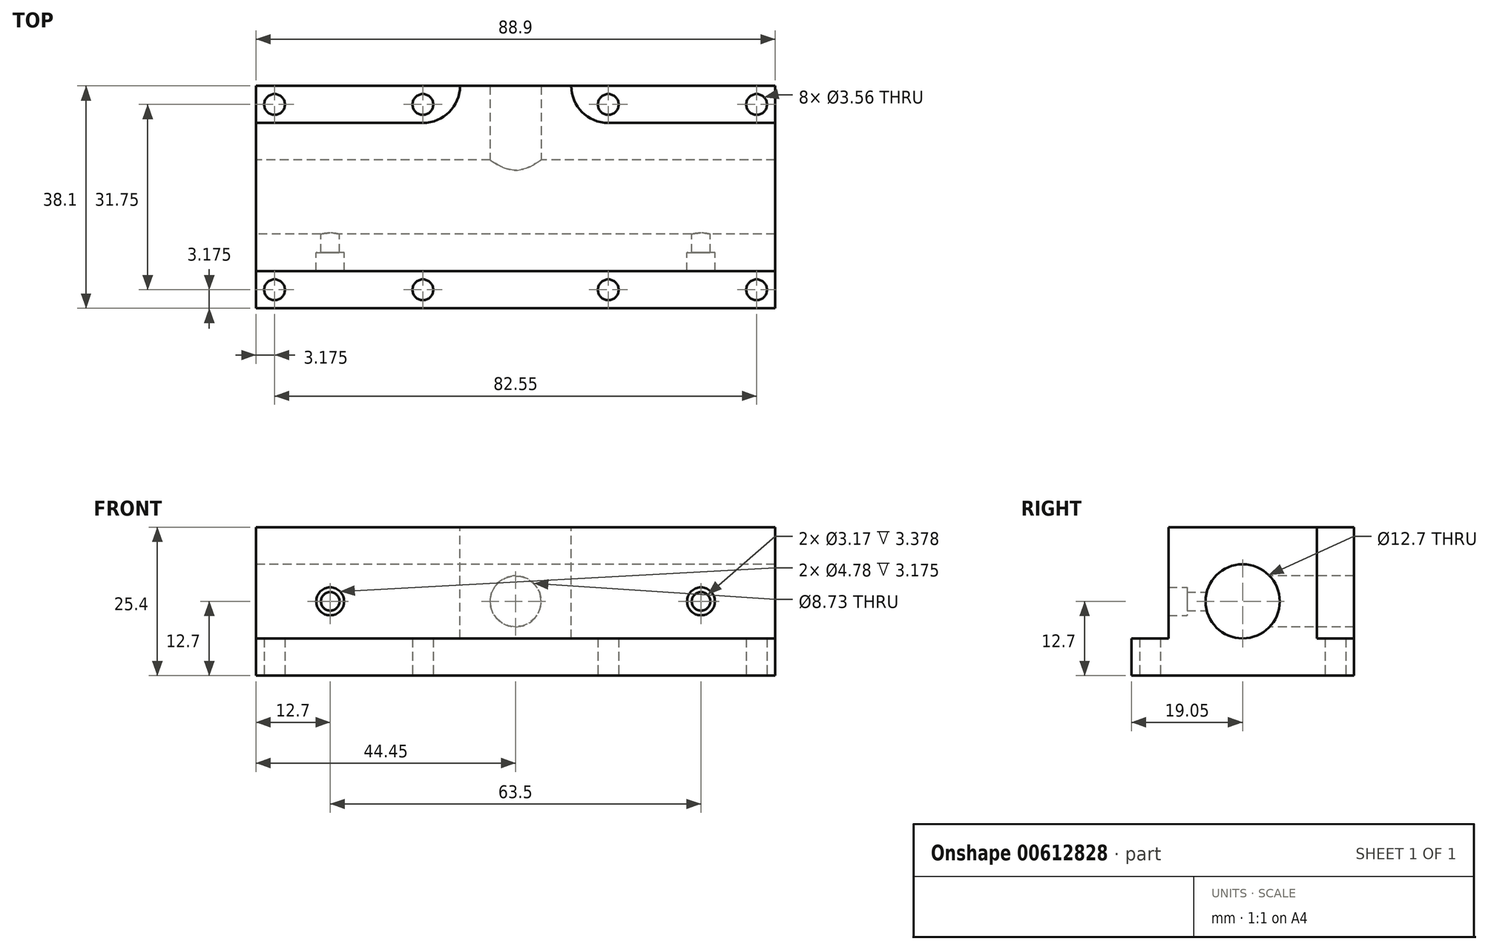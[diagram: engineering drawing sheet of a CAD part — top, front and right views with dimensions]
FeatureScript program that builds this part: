
annotation { "Feature Type Name" : "Feature", "Feature Type Description" : "" }
export const myFeature = defineFeature(function(context is Context, id is Id, definition is map)
    precondition{}
    {
        {
            var Q0;
            Q0=qCreatedBy(makeId("Right.planeOp"),FACE);
            var sketch = newSketch(context, id + "F0", { "sketchPlane" : qUnion([Q0])});
            skLineSegment(sketch, "E0.bottom", {"start": v(-19.05, -12.7) * mm, "end": v(19.05, -12.7) * mm});
            skLineSegment(sketch, "E0.top", {"start": v(-19.05, 12.7) * mm, "end": v(19.05, 12.7) * mm});
            skLineSegment(sketch, "E0.left", {"start": v(-19.05, -12.7) * mm, "end": v(-19.05, 12.7) * mm});
            skLineSegment(sketch, "E0.right", {"start": v(19.05, -12.7) * mm, "end": v(19.05, 12.7) * mm});
            skPoint(sketch, "E1", {"position": v(0, 12.7) * mm});
            skPoint(sketch, "E2", {"position": v(19.05, 0) * mm});
            skCircle(sketch, "E3", {"center": v(0, 0) * mm, "radius": 6.35 * mm});
            skSolve(sketch);
        }
        {
            var Q0;
            Q0=qSketchRegion(id+"F0",true);
            extrude(context, id + "F1", {"entities" : qUnion([Q0]), "depth" : 88.9 * mm, "symmetric" : true});
        }
        {
            var Q0;
            Q0=makeQuery(id+"F1.opExtrude","SWEPT_FACE",FACE,{"disambiguationData":[OSD([sQuery(id+"F0.wireOp",EDGE,"E0.top")])]});
            var sketch = newSketch(context, id + "F2", { "sketchPlane" : qUnion([Q0])});
            skLineSegment(sketch, "E4.bottom", {"start": v(-44.45, 19.05) * mm, "end": v(-9.53, 19.05) * mm});
            skLineSegment(sketch, "E4.top", {"start": v(-44.45, 12.7) * mm, "end": v(-15.87, 12.7) * mm});
            skLineSegment(sketch, "E4.left", {"start": v(-44.45, 19.05) * mm, "end": v(-44.45, 12.7) * mm});
            skLineSegment(sketch, "E4.right", {"start": v(44.45, 19.05) * mm, "end": v(44.45, 12.7) * mm});
            skLineSegment(sketch, "E5.bottom", {"start": v(-44.45, -19.05) * mm, "end": v(44.45, -19.05) * mm});
            skLineSegment(sketch, "E5.top", {"start": v(-44.45, -12.7) * mm, "end": v(44.45, -12.7) * mm});
            skLineSegment(sketch, "E5.left", {"start": v(-44.45, -19.05) * mm, "end": v(-44.45, -12.7) * mm});
            skLineSegment(sketch, "E5.right", {"start": v(44.45, -19.05) * mm, "end": v(44.45, -12.7) * mm});
            skLineSegment(sketch, "E6.trimOffspring", {"start": v(15.87, 12.7) * mm, "end": v(44.45, 12.7) * mm});
            skLineSegment(sketch, "E7.trimOffspring", {"start": v(9.52, 19.05) * mm, "end": v(44.45, 19.05) * mm});
            skArc(sketch, "E8", {"start": v(-9.52, 19.05) * mm, "mid": v(-11.38, 14.56) * mm, "end": v(-15.87, 12.7) * mm});
            skArc(sketch, "E9", {"start": v(9.52, 19.05) * mm, "mid": v(11.38, 14.56) * mm, "end": v(15.87, 12.7) * mm});
            skSolve(sketch);
        }
        {
            var Q0;
            Q0=qSketchRegion(id+"F2",true);
            extrude(context, id + "F3", {"entities" : qUnion([Q0]), "operationType" : NewBodyOperationType.REMOVE, "oppositeDirection" : true, "depth" : 19.05 * mm});
        }
        {
            var Q0;
            Q0=makeQuery(id+"F1.opExtrude","SWEPT_FACE",FACE,{"disambiguationData":[OSD([sQuery(id+"F0.wireOp",EDGE,"E0.right")])]});
            var sketch = newSketch(context, id + "F4", { "sketchPlane" : qUnion([Q0])});
            skPoint(sketch, "E10", {"position": v(0, 0) * mm});
            skSolve(sketch);
        }
        {
            var Q0;
            Q0=sQuery(id+"F4.wireOp",VERTEX,"E10");
            var Q1;
            Q1=makeQuery(id+"F1.opExtrude","SWEPT_BODY",BODY,{"disambiguationData":[OSD([sQuery(id+"F0.wireOp",EDGE,"E0.bottom"),sQuery(id+"F0.wireOp",EDGE,"E0.top"),sQuery(id+"F0.wireOp",EDGE,"E0.left"),sQuery(id+"F0.wireOp",EDGE,"E0.right"),sQuery(id+"F0.wireOp",EDGE,"E3")])]});
            hole(context, id + "F5", {"style" : HoleStyle.SIMPLE, "holeDiameter" : 8.73 * mm, "endStyle" : HoleEndStyle.BLIND, "holeDepth" : 19.05 * mm, "locations" : qUnion([Q0]), "scope" : qUnion([Q1])});
        }
        {
            var Q0;
            Q0=makeQuery(id+"F3.boolean.opBoolean","COPY",FACE,{"derivedFrom":makeQuery(id+"F3.opExtrude","SWEPT_FACE",FACE,{"disambiguationData":[OSD([sQuery(id+"F2.wireOp",EDGE,"E5.top")])]})});
            var sketch = newSketch(context, id + "F6", { "sketchPlane" : qUnion([Q0])});
            skPoint(sketch, "E11", {"position": v(-31.75, 0) * mm});
            skPoint(sketch, "E12", {"position": v(31.75, 0) * mm});
            skSolve(sketch);
        }
        {
            var Q0;
            Q0=sQuery(id+"F6.wireOp",VERTEX,"E11");
            var Q1;
            Q1=sQuery(id+"F6.wireOp",VERTEX,"E12");
            var Q2;
            Q2=makeQuery(id+"F1.opExtrude","SWEPT_BODY",BODY,{"disambiguationData":[OSD([sQuery(id+"F0.wireOp",EDGE,"E0.bottom"),sQuery(id+"F0.wireOp",EDGE,"E0.top"),sQuery(id+"F0.wireOp",EDGE,"E0.left"),sQuery(id+"F0.wireOp",EDGE,"E0.right"),sQuery(id+"F0.wireOp",EDGE,"E3")])]});
            hole(context, id + "F7", {"style" : HoleStyle.C_BORE, "holeDiameter" : 3.17 * mm, "cBoreDiameter" : 4.78 * mm, "cBoreDepth" : 3.17 * mm, "endStyle" : HoleEndStyle.BLIND, "holeDepth" : 12.7 * mm, "locations" : qUnion([Q0, Q1]), "scope" : qUnion([Q2])});
        }
        {
            var Q0;
            Q0=makeQuery(id+"F3.boolean.opBoolean","COPY",FACE,{"derivedFrom":makeQuery(id+"F3.opExtrude","CAP_FACE",FACE,{"disambiguationData":[OSD([sQuery(id+"F2.wireOp",EDGE,"E5.bottom"),sQuery(id+"F2.wireOp",EDGE,"E5.top"),sQuery(id+"F2.wireOp",EDGE,"E5.left"),sQuery(id+"F2.wireOp",EDGE,"E5.right")])],"isStart":false})});
            var sketch = newSketch(context, id + "F8", { "sketchPlane" : qUnion([Q0])});
            skPoint(sketch, "E13", {"position": v(-41.28, 15.88) * mm});
            skPoint(sketch, "E14", {"position": v(-15.88, 15.88) * mm});
            skPoint(sketch, "E15", {"position": v(15.87, 15.88) * mm});
            skPoint(sketch, "E16", {"position": v(41.27, 15.88) * mm});
            skPoint(sketch, "E17", {"position": v(-41.28, -15.88) * mm});
            skPoint(sketch, "E18", {"position": v(-15.88, -15.88) * mm});
            skPoint(sketch, "E19", {"position": v(15.87, -15.88) * mm});
            skPoint(sketch, "E20", {"position": v(41.27, -15.88) * mm});
            skSolve(sketch);
        }
        {
            var Q0;
            Q0=sQuery(id+"F8.wireOp",VERTEX,"E13");
            var Q1;
            Q1=sQuery(id+"F8.wireOp",VERTEX,"E14");
            var Q2;
            Q2=sQuery(id+"F8.wireOp",VERTEX,"E15");
            var Q3;
            Q3=sQuery(id+"F8.wireOp",VERTEX,"E16");
            var Q4;
            Q4=sQuery(id+"F8.wireOp",VERTEX,"E20");
            var Q5;
            Q5=sQuery(id+"F8.wireOp",VERTEX,"E19");
            var Q6;
            Q6=sQuery(id+"F8.wireOp",VERTEX,"E18");
            var Q7;
            Q7=sQuery(id+"F8.wireOp",VERTEX,"E17");
            var Q8;
            Q8=makeQuery(id+"F1.opExtrude","SWEPT_BODY",BODY,{"disambiguationData":[OSD([sQuery(id+"F0.wireOp",EDGE,"E0.bottom"),sQuery(id+"F0.wireOp",EDGE,"E0.top"),sQuery(id+"F0.wireOp",EDGE,"E0.left"),sQuery(id+"F0.wireOp",EDGE,"E0.right"),sQuery(id+"F0.wireOp",EDGE,"E3")])]});
            hole(context, id + "F9", {"style" : HoleStyle.SIMPLE, "holeDiameter" : 3.56 * mm, "endStyle" : HoleEndStyle.THROUGH, "locations" : qUnion([Q0, Q1, Q2, Q3, Q4, Q5, Q6, Q7]), "scope" : qUnion([Q8])});
        }
    });
